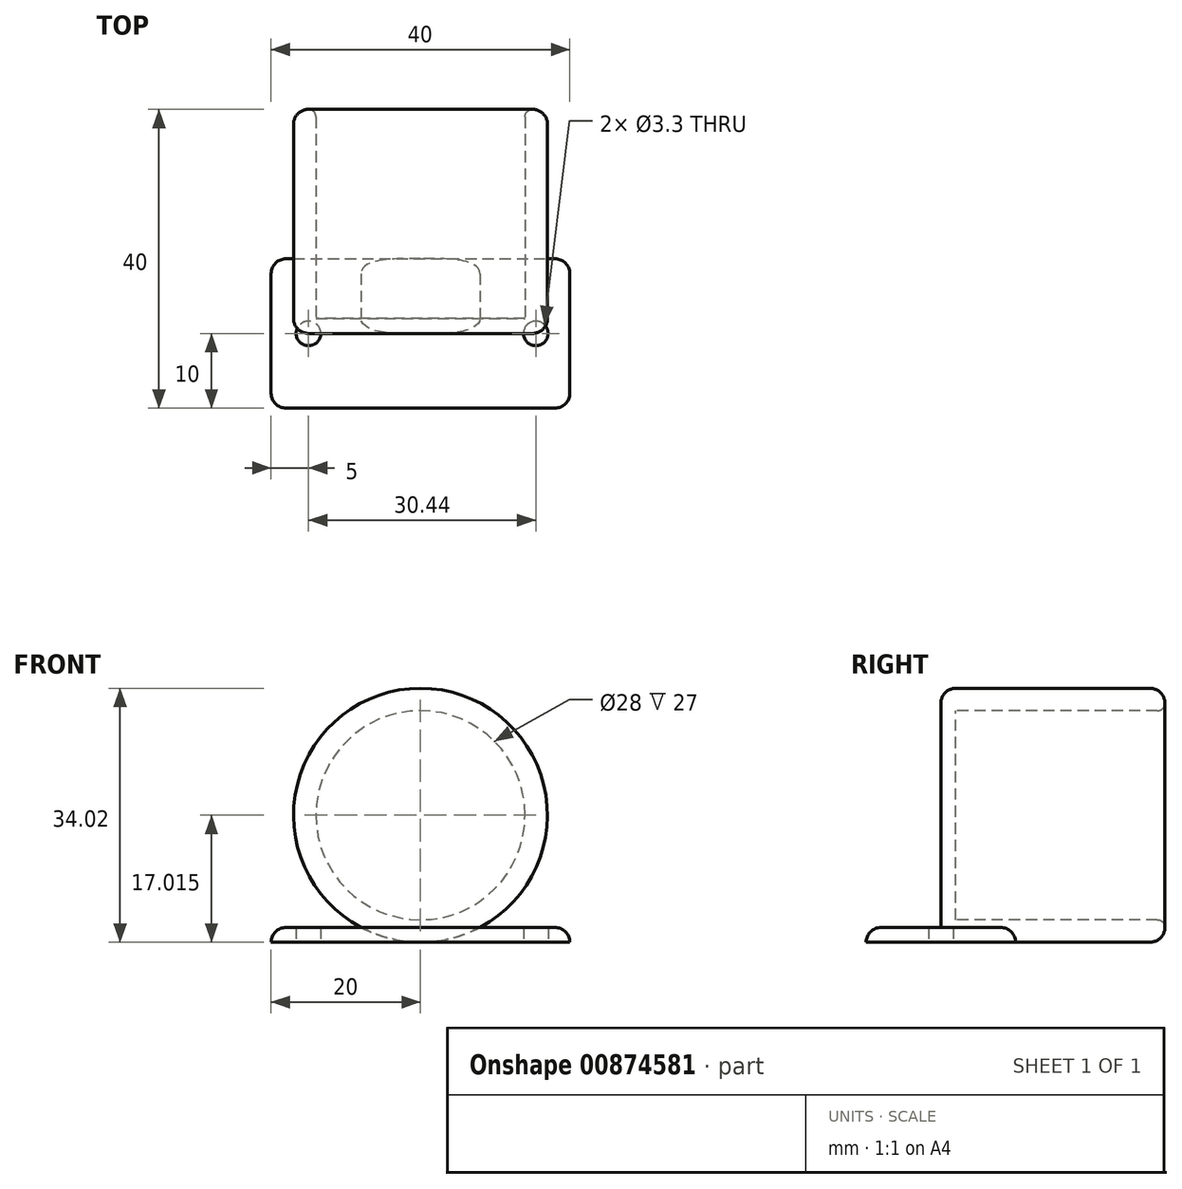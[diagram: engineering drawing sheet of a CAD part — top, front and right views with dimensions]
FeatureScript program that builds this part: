
annotation { "Feature Type Name" : "Feature", "Feature Type Description" : "" }
export const myFeature = defineFeature(function(context is Context, id is Id, definition is map)
    precondition{}
    {
        {
            var Q0;
            Q0=qCreatedBy(makeId("Top.planeOp"),FACE);
            var sketch = newSketch(context, id + "F0", { "sketchPlane" : qUnion([Q0])});
            skLineSegment(sketch, "E0.bottom", {"start": v(-20, 10) * mm, "end": v(20, 10) * mm});
            skLineSegment(sketch, "E0.top", {"start": v(-20, -10) * mm, "end": v(20, -10) * mm});
            skLineSegment(sketch, "E0.left", {"start": v(-20, 10) * mm, "end": v(-20, -10) * mm});
            skLineSegment(sketch, "E0.right", {"start": v(20, 10) * mm, "end": v(20, -10) * mm});
            skPoint(sketch, "E0.middle", {"position": v(0, 0) * mm});
            skPoint(sketch, "E1", {"position": v(-15, 0) * mm});
            skPoint(sketch, "E2", {"position": v(15.44, 0) * mm});
            skSolve(sketch);
        }
        {
            var Q0;
            Q0=makeQuery(id+"F0.imprint","IMPRINT",FACE,{"disambiguationData":[TD([[makeQuery(id+"F0.imprint","IMPRINT",EDGE,{"derivedFrom":sQuery(id+"F0.wireOp",EDGE,"E0.bottom")}),-1.0]])]});
            extrude(context, id + "F1", {"entities" : qUnion([Q0]), "depth" : 2 * mm, "offsetDistance" : 25 * mm});
        }
        {
            var Q0;
            Q0=sQuery(id+"F0.wireOp",VERTEX,"E1");
            var Q1;
            Q1=sQuery(id+"F0.wireOp",VERTEX,"E2");
            var Q2;
            Q2=makeQuery(id+"F1.opExtrude","SWEPT_BODY",BODY,{"disambiguationData":[OSD([sQuery(id+"F0.wireOp",EDGE,"E0.bottom"),sQuery(id+"F0.wireOp",EDGE,"E0.top"),sQuery(id+"F0.wireOp",EDGE,"E0.left"),sQuery(id+"F0.wireOp",EDGE,"E0.right")])]});
            hole(context, id + "F2", {"style" : HoleStyle.SIMPLE, "endStyle" : HoleEndStyle.BLIND, "oppositeDirection" : true, "standardTappedOrClearance" : lookupTablePath({ "fit" : "Normal", "standard" : "ISO", "size" : "M3", "type" : "Clearance" }), "standardBlindInLast" : lookupTablePath({ "fit" : "Standard", "standard" : "ISO", "size" : "M3", "type" : "Clearance" }), "holeDiameter" : 3.3 * mm, "majorDiameter" : 5 * mm, "holeDepth" : 6 * mm, "isTappedThrough" : true, "tappedDepth" : 12 * mm, "tapClearance" : 3, "locations" : qUnion([Q0, Q1]), "scope" : qUnion([Q2])});
        }
        {
            var Q0;
            Q0=qCreatedBy(makeId("Front.planeOp"),FACE);
            var sketch = newSketch(context, id + "F3", { "sketchPlane" : qUnion([Q0])});
            skCircle(sketch, "E3", {"center": v(0, 17.02) * mm, "radius": 14 * mm});
            skCircle(sketch, "E4", {"center": v(0, 17.02) * mm, "radius": 17 * mm});
            skSolve(sketch);
        }
        {
            var Q0;
            Q0=makeQuery(id+"F3.imprint","IMPRINT",FACE,{"disambiguationData":[TD([[makeQuery(id+"F3.imprint","IMPRINT",EDGE,{"derivedFrom":sQuery(id+"F3.wireOp",EDGE,"E3")}),-1.0]])]});
            extrude(context, id + "F4", {"entities" : qUnion([Q0]), "operationType" : NewBodyOperationType.ADD, "oppositeDirection" : true, "depth" : 30 * mm, "offsetDistance" : 25 * mm});
        }
        {
            var Q0;
            Q0=makeQuery(id+"F3.imprint","IMPRINT",FACE,{"disambiguationData":[TD([[makeQuery(id+"F3.imprint","IMPRINT",EDGE,{"derivedFrom":sQuery(id+"F3.wireOp",EDGE,"E3")}),1.0]])]});
            extrude(context, id + "F5", {"entities" : qUnion([Q0]), "operationType" : NewBodyOperationType.ADD, "oppositeDirection" : true, "depth" : 2 * mm, "offsetDistance" : 25 * mm});
        }
        {
            var Q0;
            Q0=makeQuery(id+"F4.opExtrude","CAP_EDGE",EDGE,{"disambiguationData":[OSD([sQuery(id+"F3.wireOp",EDGE,"E4")])],"isStart":true});
            var Q1;
            Q1=makeQuery(id+"F4.opExtrude","CAP_EDGE",EDGE,{"disambiguationData":[OSD([sQuery(id+"F3.wireOp",EDGE,"E4")])],"isStart":false});
            fillet(context, id + "F6", {"entities" : qUnion([Q0, Q1]), "radius" : 2 * mm, "tangentPropagation" : true, "allowEdgeOverflow" : false});
        }
        {
            var Q0;
            Q0=makeQuery(id+"F4.opExtrude","CAP_EDGE",EDGE,{"disambiguationData":[OSD([sQuery(id+"F3.wireOp",EDGE,"E3")])],"isStart":false});
            fillet(context, id + "F7", {"entities" : qUnion([Q0]), "radius" : 1 * mm, "tangentPropagation" : true, "allowEdgeOverflow" : false});
        }
        {
            var Q0;
            Q0=makeQuery(id+"F1.opExtrude","SWEPT_EDGE",EDGE,{"disambiguationData":[OSD([sQuery(id+"F0.wireOp",EDGE,"E0.bottom"),sQuery(id+"F0.wireOp",EDGE,"E0.right")])]});
            var Q1;
            Q1=makeQuery(id+"F1.opExtrude","SWEPT_EDGE",EDGE,{"disambiguationData":[OSD([sQuery(id+"F0.wireOp",EDGE,"E0.top"),sQuery(id+"F0.wireOp",EDGE,"E0.right")])]});
            var Q2;
            Q2=makeQuery(id+"F1.opExtrude","SWEPT_EDGE",EDGE,{"disambiguationData":[OSD([sQuery(id+"F0.wireOp",EDGE,"E0.bottom"),sQuery(id+"F0.wireOp",EDGE,"E0.left")])]});
            var Q3;
            Q3=makeQuery(id+"F1.opExtrude","SWEPT_EDGE",EDGE,{"disambiguationData":[OSD([sQuery(id+"F0.wireOp",EDGE,"E0.top"),sQuery(id+"F0.wireOp",EDGE,"E0.left")])]});
            fillet(context, id + "F8", {"entities" : qUnion([Q0, Q1, Q2, Q3]), "radius" : 2 * mm, "tangentPropagation" : true, "allowEdgeOverflow" : false});
        }
        {
            var Q0;
            {var subQ0=sQuery(id+"F0.wireOp",EDGE,"E0.bottom");var subQ1=sQuery(id+"F0.wireOp",EDGE,"E0.left");Q0=makeQuery(id+"F4.boolean.opBoolean","SPLIT",EDGE,{"disambiguationData":[TD([makeQuery(id+"F1.opExtrude","SWEPT_FACE",FACE,{"disambiguationData":[OSD([subQ1])]})])],"derivedFrom":makeQuery(id+"F1.opExtrude","CAP_EDGE",EDGE,{"disambiguationData":[OSD([subQ0])],"isStart":false})});}
            fillet(context, id + "F9", {"entities" : qUnion([Q0]), "radius" : 2 * mm, "tangentPropagation" : true, "allowEdgeOverflow" : false});
        }
    });
